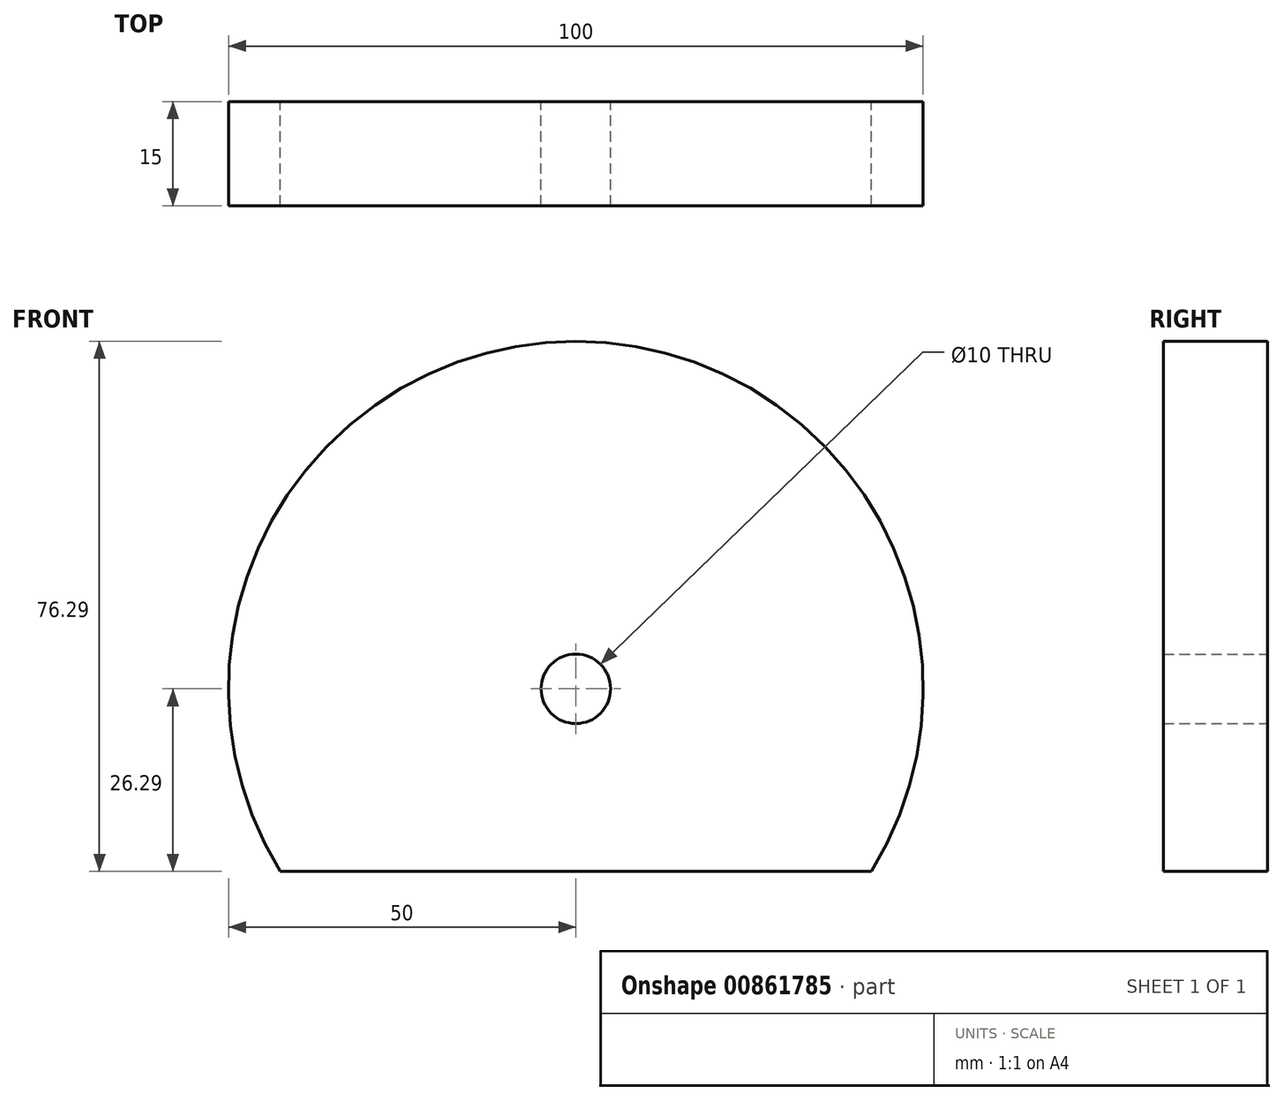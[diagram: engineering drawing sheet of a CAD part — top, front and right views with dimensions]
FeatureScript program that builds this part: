
annotation { "Feature Type Name" : "Feature", "Feature Type Description" : "" }
export const myFeature = defineFeature(function(context is Context, id is Id, definition is map)
    precondition{}
    {
        {
            var Q0;
            Q0=qCreatedBy(makeId("Front.planeOp"),FACE);
            var sketch = newSketch(context, id + "F0", { "sketchPlane" : qUnion([Q0])});
            skCircle(sketch, "E0", {"center": v(0, 0) * mm, "radius": 50 * mm});
            skCircle(sketch, "E1", {"center": v(0, 0) * mm, "radius": 5 * mm});
            skLineSegment(sketch, "E2", {"start": v(-42.53, -26.29) * mm, "end": v(42.53, -26.29) * mm});
            skSolve(sketch);
        }
        {
            var Q0;
            Q0=makeQuery(id+"F0.imprint","IMPRINT",FACE,{"disambiguationData":[TD([[makeQuery(id+"F0.imprint","IMPRINT",EDGE,{"derivedFrom":sQuery(id+"F0.wireOp",EDGE,"E1")}),-1.0]])]});
            extrude(context, id + "F1", {"entities" : qUnion([Q0]), "depth" : 15 * mm, "offsetDistance" : 25 * mm});
        }
    });
